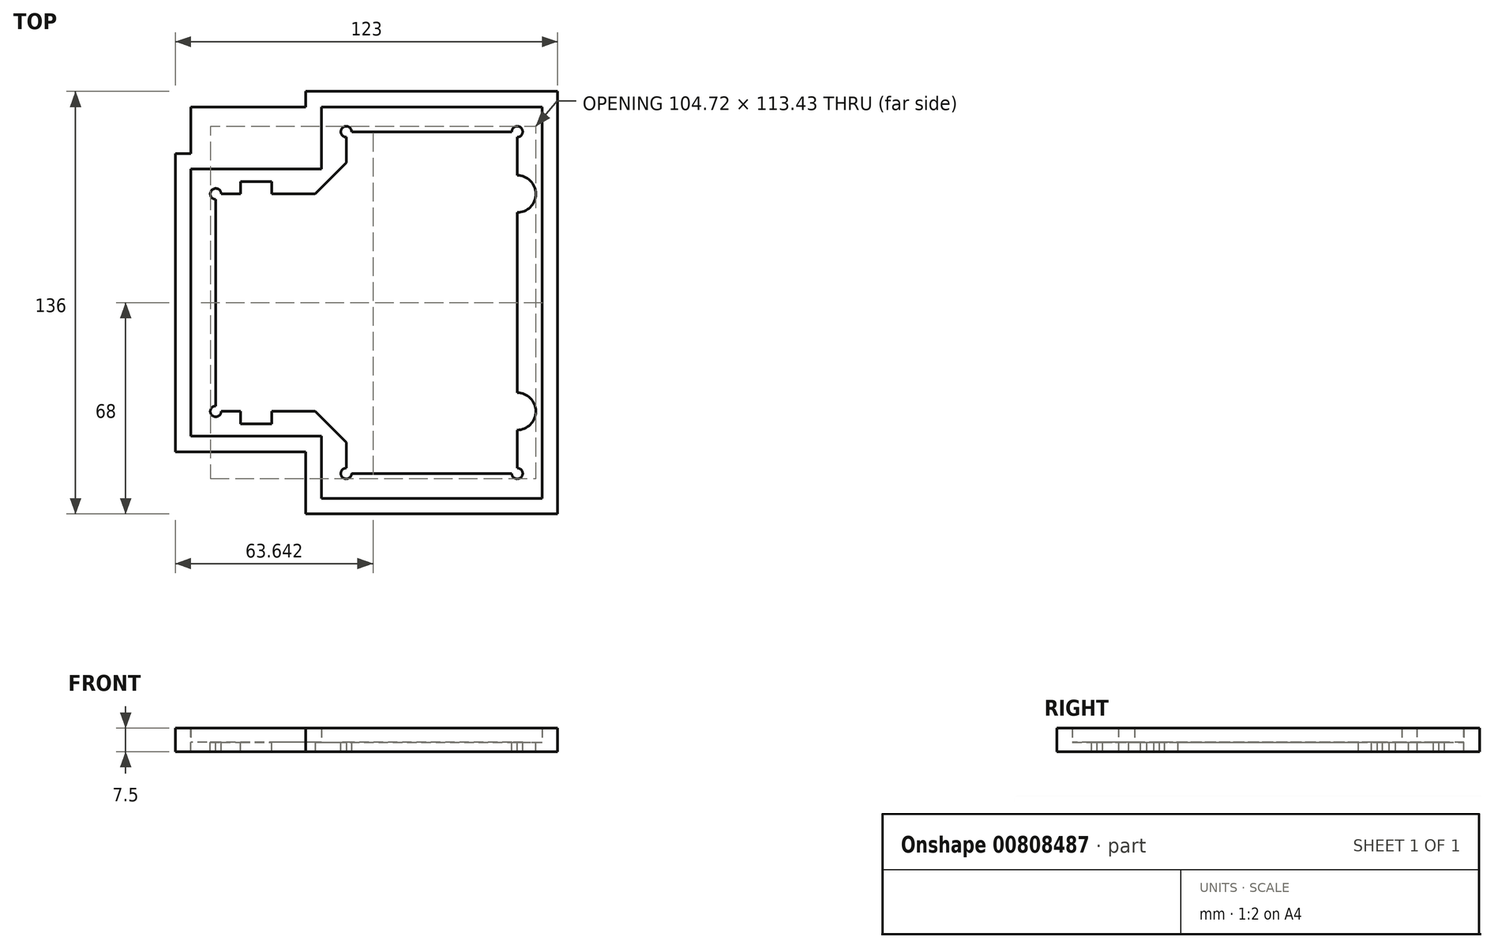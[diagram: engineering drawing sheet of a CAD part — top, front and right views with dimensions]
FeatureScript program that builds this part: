
annotation { "Feature Type Name" : "Feature", "Feature Type Description" : "" }
export const myFeature = defineFeature(function(context is Context, id is Id, definition is map)
    precondition{}
    {
        {
            var Q0;
            Q0=qCreatedBy(makeId("Top.planeOp"),FACE);
            var sketch = newSketch(context, id + "F0", { "sketchPlane" : qUnion([Q0])});
            skLineSegment(sketch, "E0.bottom", {"start": v(-56.5, 63) * mm, "end": v(56.5, 63) * mm});
            skLineSegment(sketch, "E0.top", {"start": v(-56.5, -63) * mm, "end": v(56.5, -63) * mm});
            skLineSegment(sketch, "E0.left", {"start": v(-56.5, 63) * mm, "end": v(-56.5, -63) * mm});
            skLineSegment(sketch, "E0.right", {"start": v(56.5, 63) * mm, "end": v(56.5, -63) * mm});
            skPoint(sketch, "E0.middle", {"position": v(0, 0) * mm});
            skLineSegment(sketch, "E1.bottom", {"start": v(-56.5, 63) * mm, "end": v(-14.5, 63) * mm});
            skLineSegment(sketch, "E1.top", {"start": v(-56.5, 43) * mm, "end": v(-14.5, 43) * mm});
            skLineSegment(sketch, "E1.left", {"start": v(-56.5, 63) * mm, "end": v(-56.5, 43) * mm});
            skLineSegment(sketch, "E1.right", {"start": v(-14.5, 63) * mm, "end": v(-14.5, 43) * mm});
            skLineSegment(sketch, "E2.bottom", {"start": v(-56.5, -63) * mm, "end": v(-14.5, -63) * mm});
            skLineSegment(sketch, "E2.top", {"start": v(-56.5, -43) * mm, "end": v(-14.5, -43) * mm});
            skLineSegment(sketch, "E2.left", {"start": v(-56.5, -63) * mm, "end": v(-56.5, -43) * mm});
            skLineSegment(sketch, "E2.right", {"start": v(-14.5, -63) * mm, "end": v(-14.5, -43) * mm});
            skSolve(sketch);
        }
        {
            var Q0;
            Q0=makeQuery(id+"F0.imprint","IMPRINT",FACE,{"disambiguationData":[TD([[makeQuery(id+"F0.imprint","IMPRINT",EDGE,{"derivedFrom":sQuery(id+"F0.wireOp",EDGE,"E0.bottom")}),-1.0]])]});
            extrude(context, id + "F1", {"entities" : qUnion([Q0]), "depth" : 3 * mm, "offsetDistance" : 25 * mm});
        }
        {
            var Q0;
            Q0=makeQuery(id+"F1.opExtrude","CAP_FACE",FACE,{"disambiguationData":[OSD([sQuery(id+"F0.wireOp",EDGE,"E0.bottom"),sQuery(id+"F0.wireOp",EDGE,"E0.top"),sQuery(id+"F0.wireOp",EDGE,"E0.left"),sQuery(id+"F0.wireOp",EDGE,"E0.right"),sQuery(id+"F0.wireOp",EDGE,"E1.top"),sQuery(id+"F0.wireOp",EDGE,"E1.right"),sQuery(id+"F0.wireOp",EDGE,"E2.top"),sQuery(id+"F0.wireOp",EDGE,"E2.right")])],"isStart":false});
            var sketch = newSketch(context, id + "F2", { "sketchPlane" : qUnion([Q0])});
            skLineSegment(sketch, "E3.0", {"start": v(61.5, -68) * mm, "end": v(61.5, 68) * mm});
            skLineSegment(sketch, "E3.1", {"start": v(-19.5, -68) * mm, "end": v(61.5, -68) * mm});
            skLineSegment(sketch, "E3.2", {"start": v(61.5, 68) * mm, "end": v(-19.5, 68) * mm});
            skLineSegment(sketch, "E3.3", {"start": v(-19.5, -48) * mm, "end": v(-19.5, -68) * mm});
            skLineSegment(sketch, "E3.4", {"start": v(-19.5, 68) * mm, "end": v(-19.5, 48) * mm});
            skLineSegment(sketch, "E3.5", {"start": v(-19.5, 48) * mm, "end": v(-61.5, 48) * mm});
            skLineSegment(sketch, "E3.6", {"start": v(-61.5, 48) * mm, "end": v(-61.5, -48) * mm});
            skLineSegment(sketch, "E3.7", {"start": v(-61.5, -48) * mm, "end": v(-19.5, -48) * mm});
            skSolve(sketch);
        }
        {
            var Q0;
            Q0=makeQuery(id+"F2.imprint","IMPRINT",FACE,{"disambiguationData":[TD([[makeQuery(id+"F2.imprint","IMPRINT",EDGE,{"derivedFrom":sQuery(id+"F2.wireOp",EDGE,"E3.0")}),1.0]])]});
            var Q1;
            Q1=makeQuery(id+"F1.opExtrude","CAP_FACE",FACE,{"disambiguationData":[OSD([sQuery(id+"F0.wireOp",EDGE,"E0.bottom"),sQuery(id+"F0.wireOp",EDGE,"E0.top"),sQuery(id+"F0.wireOp",EDGE,"E0.left"),sQuery(id+"F0.wireOp",EDGE,"E0.right"),sQuery(id+"F0.wireOp",EDGE,"E1.top"),sQuery(id+"F0.wireOp",EDGE,"E1.right"),sQuery(id+"F0.wireOp",EDGE,"E2.top"),sQuery(id+"F0.wireOp",EDGE,"E2.right")])],"isStart":true});
            extrude(context, id + "F3", {"entities" : qUnion([Q0]), "operationType" : NewBodyOperationType.ADD, "endBound" : BoundingType.UP_TO_SURFACE, "oppositeDirection" : true, "depth" : 25 * mm, "endBoundEntityFace" : qUnion([Q1]), "offsetDistance" : 25 * mm});
        }
        {
            var Q0;
            {var subQ0=sQuery(id+"F0.wireOp",EDGE,"E2.right");var subQ1=sQuery(id+"F0.wireOp",EDGE,"E2.top");var subQ2=sQuery(id+"F0.wireOp",EDGE,"E1.right");var subQ3=sQuery(id+"F0.wireOp",EDGE,"E1.top");var subQ4=sQuery(id+"F0.wireOp",EDGE,"E0.right");var subQ5=sQuery(id+"F0.wireOp",EDGE,"E0.left");var subQ6=sQuery(id+"F0.wireOp",EDGE,"E0.top");var subQ7=sQuery(id+"F0.wireOp",EDGE,"E0.bottom");Q0=makeQuery(id+"F3.boolean.opBoolean","MERGE",FACE,{"derivedFrom":[makeQuery(id+"F1.opExtrude","CAP_FACE",FACE,{"disambiguationData":[OSD([subQ7,subQ6,subQ5,subQ4,subQ3,subQ2,subQ1,subQ0])],"isStart":false}),makeQuery(id+"F3.opExtrude","CAP_FACE",FACE,{"disambiguationData":[OSD([subQ7,subQ6,subQ5,subQ4,subQ3,subQ2,subQ1,subQ0,sQuery(id+"F2.wireOp",EDGE,"E3.0"),sQuery(id+"F2.wireOp",EDGE,"E3.1"),sQuery(id+"F2.wireOp",EDGE,"E3.2"),sQuery(id+"F2.wireOp",EDGE,"E3.3"),sQuery(id+"F2.wireOp",EDGE,"E3.4"),sQuery(id+"F2.wireOp",EDGE,"E3.5"),sQuery(id+"F2.wireOp",EDGE,"E3.6"),sQuery(id+"F2.wireOp",EDGE,"E3.7")])],"isStart":true})]});}
            var sketch = newSketch(context, id + "F4", { "sketchPlane" : qUnion([Q0])});
            skLineSegment(sketch, "E4.0", {"start": v(-6.5, 35) * mm, "end": v(-48.5, 35) * mm});
            skLineSegment(sketch, "E4.1", {"start": v(-6.5, 55) * mm, "end": v(-6.5, 35) * mm});
            skLineSegment(sketch, "E4.2", {"start": v(-48.5, 35) * mm, "end": v(-48.5, -35) * mm});
            skLineSegment(sketch, "E4.3", {"start": v(48.5, 55) * mm, "end": v(-6.5, 55) * mm});
            skLineSegment(sketch, "E4.4", {"start": v(-48.5, -35) * mm, "end": v(-6.5, -35) * mm});
            skLineSegment(sketch, "E4.5", {"start": v(-6.5, -35) * mm, "end": v(-6.5, -55) * mm});
            skLineSegment(sketch, "E4.6", {"start": v(-6.5, -55) * mm, "end": v(48.5, -55) * mm});
            skLineSegment(sketch, "E4.7", {"start": v(48.5, -55) * mm, "end": v(48.5, 55) * mm});
            skSolve(sketch);
        }
        {
            var Q0;
            Q0=makeQuery(id+"F4.imprint","IMPRINT",FACE,{"disambiguationData":[TD([[makeQuery(id+"F4.imprint","IMPRINT",EDGE,{"derivedFrom":sQuery(id+"F4.wireOp",EDGE,"E4.0")}),1.0]])]});
            extrude(context, id + "F5", {"entities" : qUnion([Q0]), "operationType" : NewBodyOperationType.REMOVE, "endBound" : BoundingType.THROUGH_ALL, "oppositeDirection" : true, "depth" : 25 * mm, "offsetDistance" : 25 * mm});
        }
        {
            var Q0;
            {var subQ0=sQuery(id+"F0.wireOp",EDGE,"E2.right");var subQ1=sQuery(id+"F0.wireOp",EDGE,"E2.top");var subQ2=sQuery(id+"F0.wireOp",EDGE,"E1.right");var subQ3=sQuery(id+"F0.wireOp",EDGE,"E1.top");var subQ4=sQuery(id+"F0.wireOp",EDGE,"E0.right");var subQ5=sQuery(id+"F0.wireOp",EDGE,"E0.left");var subQ6=sQuery(id+"F0.wireOp",EDGE,"E0.top");var subQ7=sQuery(id+"F0.wireOp",EDGE,"E0.bottom");Q0=makeQuery(id+"F3.boolean.opBoolean","MERGE",FACE,{"derivedFrom":[makeQuery(id+"F1.opExtrude","CAP_FACE",FACE,{"disambiguationData":[OSD([subQ7,subQ6,subQ5,subQ4,subQ3,subQ2,subQ1,subQ0])],"isStart":false}),makeQuery(id+"F3.opExtrude","CAP_FACE",FACE,{"disambiguationData":[OSD([subQ7,subQ6,subQ5,subQ4,subQ3,subQ2,subQ1,subQ0,sQuery(id+"F2.wireOp",EDGE,"E3.0"),sQuery(id+"F2.wireOp",EDGE,"E3.1"),sQuery(id+"F2.wireOp",EDGE,"E3.2"),sQuery(id+"F2.wireOp",EDGE,"E3.3"),sQuery(id+"F2.wireOp",EDGE,"E3.4"),sQuery(id+"F2.wireOp",EDGE,"E3.5"),sQuery(id+"F2.wireOp",EDGE,"E3.6"),sQuery(id+"F2.wireOp",EDGE,"E3.7")])],"isStart":true})]});}
            var sketch = newSketch(context, id + "F6", { "sketchPlane" : qUnion([Q0])});
            skCircle(sketch, "E5", {"center": v(-48.5, 35) * mm, "radius": 1.75 * mm});
            skCircle(sketch, "E6", {"center": v(-6.5, 55) * mm, "radius": 1.75 * mm});
            skCircle(sketch, "E7", {"center": v(48.5, 55) * mm, "radius": 1.75 * mm});
            skCircle(sketch, "E8", {"center": v(48.5, -55) * mm, "radius": 1.75 * mm});
            skCircle(sketch, "E9", {"center": v(-6.5, -55) * mm, "radius": 1.75 * mm});
            skCircle(sketch, "E10", {"center": v(-48.5, -35) * mm, "radius": 1.75 * mm});
            skCircle(sketch, "E11", {"center": v(48.5, 35) * mm, "radius": 6 * mm});
            skLineSegment(sketch, "E12", {"start": v(0, 0) * mm, "end": v(48.5, 0) * mm, "construction": true});
            skCircle(sketch, "E13.MirrorC", {"center": v(48.5, -35) * mm, "radius": 6 * mm});
            skLineSegment(sketch, "E14", {"start": v(-35.5, 35) * mm, "end": v(-35.5, -35) * mm, "construction": true});
            skLineSegment(sketch, "E15.bottom", {"start": v(-40.5, 35) * mm, "end": v(-30.5, 35) * mm});
            skLineSegment(sketch, "E15.top", {"start": v(-40.5, 39) * mm, "end": v(-30.5, 39) * mm});
            skLineSegment(sketch, "E15.left", {"start": v(-40.5, 35) * mm, "end": v(-40.5, 39) * mm});
            skLineSegment(sketch, "E15.right", {"start": v(-30.5, 35) * mm, "end": v(-30.5, 39) * mm});
            skLineSegment(sketch, "E16.bottom", {"start": v(-40.5, -35) * mm, "end": v(-30.5, -35) * mm});
            skLineSegment(sketch, "E16.top", {"start": v(-40.5, -39) * mm, "end": v(-30.5, -39) * mm});
            skLineSegment(sketch, "E16.left", {"start": v(-40.5, -35) * mm, "end": v(-40.5, -39) * mm});
            skLineSegment(sketch, "E16.right", {"start": v(-30.5, -35) * mm, "end": v(-30.5, -39) * mm});
            skSolve(sketch);
        }
        {
            var Q0;
            Q0 = qSketchRegion(id + "F6", true);
            extrude(context, id + "F7", {"entities" : qUnion([Q0]), "operationType" : NewBodyOperationType.REMOVE, "oppositeDirection" : true, "depth" : 25 * mm, "offsetDistance" : 25 * mm});
        }
        {
            var Q0;
            {var subQ0=sQuery(id+"F0.wireOp",EDGE,"E2.right");var subQ1=sQuery(id+"F0.wireOp",EDGE,"E2.top");var subQ2=sQuery(id+"F0.wireOp",EDGE,"E1.right");var subQ3=sQuery(id+"F0.wireOp",EDGE,"E1.top");var subQ4=sQuery(id+"F0.wireOp",EDGE,"E0.right");var subQ5=sQuery(id+"F0.wireOp",EDGE,"E0.left");var subQ6=sQuery(id+"F0.wireOp",EDGE,"E0.top");var subQ7=sQuery(id+"F0.wireOp",EDGE,"E0.bottom");Q0=makeQuery(id+"F3.boolean.opBoolean","MERGE",FACE,{"derivedFrom":[makeQuery(id+"F1.opExtrude","CAP_FACE",FACE,{"disambiguationData":[OSD([subQ7,subQ6,subQ5,subQ4,subQ3,subQ2,subQ1,subQ0])],"isStart":false}),makeQuery(id+"F3.opExtrude","CAP_FACE",FACE,{"disambiguationData":[OSD([subQ7,subQ6,subQ5,subQ4,subQ3,subQ2,subQ1,subQ0,sQuery(id+"F2.wireOp",EDGE,"E3.0"),sQuery(id+"F2.wireOp",EDGE,"E3.1"),sQuery(id+"F2.wireOp",EDGE,"E3.2"),sQuery(id+"F2.wireOp",EDGE,"E3.3"),sQuery(id+"F2.wireOp",EDGE,"E3.4"),sQuery(id+"F2.wireOp",EDGE,"E3.5"),sQuery(id+"F2.wireOp",EDGE,"E3.6"),sQuery(id+"F2.wireOp",EDGE,"E3.7")])],"isStart":true})]});}
            var sketch = newSketch(context, id + "F8", { "sketchPlane" : qUnion([Q0])});
            skLineSegment(sketch, "E17.0", {"start": v(-14.5, 63) * mm, "end": v(-14.5, 43) * mm});
            skLineSegment(sketch, "E17.1", {"start": v(56.5, 63) * mm, "end": v(-14.5, 63) * mm});
            skLineSegment(sketch, "E17.2", {"start": v(-14.5, 43) * mm, "end": v(-56.5, 43) * mm});
            skLineSegment(sketch, "E17.3", {"start": v(56.5, -63) * mm, "end": v(56.5, 63) * mm});
            skLineSegment(sketch, "E17.4", {"start": v(-56.5, 43) * mm, "end": v(-56.5, -43) * mm});
            skLineSegment(sketch, "E17.5", {"start": v(-56.5, -43) * mm, "end": v(-14.5, -43) * mm});
            skLineSegment(sketch, "E17.6", {"start": v(-14.5, -43) * mm, "end": v(-14.5, -63) * mm});
            skLineSegment(sketch, "E17.7", {"start": v(-14.5, -63) * mm, "end": v(56.5, -63) * mm});
            skSolve(sketch);
        }
        {
            var Q0;
            Q0=makeQuery(id+"F8.imprint","IMPRINT",FACE,{"disambiguationData":[TD([[makeQuery(id+"F8.imprint","IMPRINT",EDGE,{"derivedFrom":sQuery(id+"F8.wireOp",EDGE,"E17.0")}),-1.0]])]});
            extrude(context, id + "F9", {"entities" : qUnion([Q0]), "operationType" : NewBodyOperationType.ADD, "depth" : 4.5 * mm, "offsetDistance" : 25 * mm});
        }
        {
            var Q0;
            {var subQ0=sQuery(id+"F0.wireOp",EDGE,"E2.right");var subQ1=sQuery(id+"F0.wireOp",EDGE,"E2.top");var subQ2=sQuery(id+"F0.wireOp",EDGE,"E1.right");var subQ3=sQuery(id+"F0.wireOp",EDGE,"E1.top");var subQ4=sQuery(id+"F0.wireOp",EDGE,"E0.right");var subQ5=sQuery(id+"F0.wireOp",EDGE,"E0.left");var subQ6=sQuery(id+"F0.wireOp",EDGE,"E0.top");var subQ7=sQuery(id+"F0.wireOp",EDGE,"E0.bottom");Q0=makeQuery(id+"F3.boolean.opBoolean","MERGE",FACE,{"derivedFrom":[makeQuery(id+"F1.opExtrude","CAP_FACE",FACE,{"disambiguationData":[OSD([subQ7,subQ6,subQ5,subQ4,subQ3,subQ2,subQ1,subQ0])],"isStart":true}),makeQuery(id+"F3.opExtrude","CAP_FACE",FACE,{"disambiguationData":[OSD([subQ7,subQ6,subQ5,subQ4,subQ3,subQ2,subQ1,subQ0,sQuery(id+"F2.wireOp",EDGE,"E3.0"),sQuery(id+"F2.wireOp",EDGE,"E3.1"),sQuery(id+"F2.wireOp",EDGE,"E3.2"),sQuery(id+"F2.wireOp",EDGE,"E3.3"),sQuery(id+"F2.wireOp",EDGE,"E3.4"),sQuery(id+"F2.wireOp",EDGE,"E3.5"),sQuery(id+"F2.wireOp",EDGE,"E3.6"),sQuery(id+"F2.wireOp",EDGE,"E3.7")])],"isStart":false})]});}
            var sketch = newSketch(context, id + "F10", { "sketchPlane" : qUnion([Q0])});
            skLineSegment(sketch, "E18", {"start": v(-6.5, 45) * mm, "end": v(-16.5, 35) * mm});
            skLineSegment(sketch, "E19", {"start": v(48.5, 0) * mm, "end": v(-48.5, 0) * mm, "construction": true});
            skLineSegment(sketch, "E20", {"start": v(-16.5, 35) * mm, "end": v(-6.5, 35) * mm});
            skLineSegment(sketch, "E21", {"start": v(-6.5, 35) * mm, "end": v(-6.5, 45) * mm});
            skLineSegment(sketch, "E22.MirrorCS", {"start": v(-6.5, -45) * mm, "end": v(-16.5, -35) * mm});
            skLineSegment(sketch, "E23.MirrorCS", {"start": v(-6.5, -35) * mm, "end": v(-6.5, -45) * mm});
            skLineSegment(sketch, "E24.MirrorCS", {"start": v(-16.5, -35) * mm, "end": v(-6.5, -35) * mm});
            skSolve(sketch);
        }
        {
            var Q0;
            Q0 = qSketchRegion(id + "F10", true);
            extrude(context, id + "F11", {"entities" : qUnion([Q0]), "operationType" : NewBodyOperationType.REMOVE, "endBound" : BoundingType.THROUGH_ALL, "oppositeDirection" : true, "depth" : 25 * mm, "offsetDistance" : 25 * mm});
        }
    });
